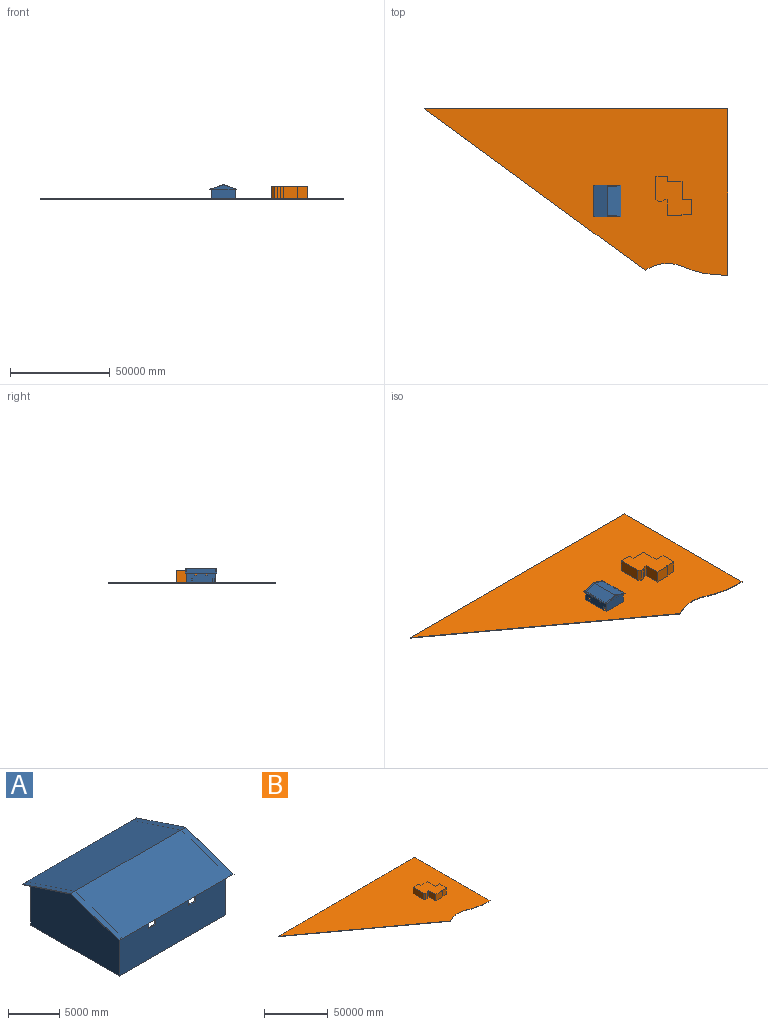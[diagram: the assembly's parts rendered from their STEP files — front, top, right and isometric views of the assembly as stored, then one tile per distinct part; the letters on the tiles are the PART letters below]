
ASSEMBLY  parts=2 mates=1
PART A: 51 faces, bbox 15849.6x13411.2x7112 mm
  f0: plane 13131.8x7065.43mm, normal (-1,0,0), area 73828293.2mm2, adj f2,f4,f8,f18,f19,f48,f49
  f1: plane 13131.8x7065.43mm, normal (1,0,0), area 51299306mm2, adj f2,f4,f5,f8,f10,f11,f12,f13
  f2: plane 14630.4x12192mm, normal (0,0,-1), area 4305959.1mm2, adj f0,f1,f3,f4,f6,f7,f8,f9
  f3: plane 14351x4876.8mm, normal (0,-1,0), area 65527610.9mm2, adj f2,f5,f6,f9,f17,f22,f23,f24
  f4: plane 14630.4x4876.8mm, normal (0,1,0), area 66890188.8mm2, adj f0,f1,f2,f5,f18,f22,f23,f24
  f5: plane 12954x2133.6mm, normal (0,0,-1), area 2088221.6mm2, adj f1,f3,f4,f6,f14,f36
  f6: plane 11912.6x4876.8mm, normal (-1,0,0), area 35566380.5mm2, adj f2,f3,f5,f7,f10,f11,f12,f13
  f7: plane 14351x4876.8mm, normal (0,1,0), area 68314702.1mm2, adj f2,f6,f9,f17,f37,f38,f39,f40
  f8: plane 14630.4x4876.8mm, normal (0,-1,0), area 69677280mm2, adj f0,f1,f2,f19,f37,f38,f39,f40
  f9: plane 11912.6x4876.8mm, normal (1,0,0), area 58095367.7mm2, adj f2,f3,f7,f17
  f10: plane 609.6x139.7mm, normal (0,0,-1), area 85161.1mm2, adj f1,f6,f12,f16
  f11: plane 4267.2x139.7mm, normal (0,1,0), area 596127.8mm2, adj f1,f2,f6,f13
  f12: plane 4267.2x139.7mm, normal (0,-1,0), area 596127.8mm2, adj f1,f6,f10,f13
  f13: plane 4876.8x139.7mm, normal (0,0,-1), area 681289mm2, adj f1,f6,f11,f12
  f14: plane 1879.6x139.7mm, normal (0,-1,0), area 262580.1mm2, adj f1,f5,f6,f15
  f15: plane 914.4x139.7mm, normal (0,0,-1), area 127741.7mm2, adj f1,f6,f14,f16
  f16: plane 1879.6x139.7mm, normal (0,1,0), area 262580.1mm2, adj f1,f6,f10,f15
  f17: plane 14351x11912.6mm, normal (0,0,-1), area 170957722.6mm2, adj f3,f6,f7,f9
  f18: plane 15849.6x609.6mm, normal (0,0,-1), area 9089014.1mm2, adj f0,f1,f4,f20,f45,f47,f48,f50
  f19: plane 15849.6x609.6mm, normal (0,0,-1), area 9089014.1mm2, adj f0,f1,f8,f21,f46,f47,f49,f50
  f20: plane 15849.6x6705.6mm, normal (0,0.32,0.95), area 112030092.6mm2, adj f18,f21,f47,f50
  f21: plane 15849.6x6705.6mm, normal (0,-0.32,0.95), area 112030092.6mm2, adj f19,f20,f47,f50
  f22: plane 914.4x139.7mm, normal (0,0,-1), area 127741.7mm2, adj f3,f4,f23,f25
  f23: plane 914.4x139.7mm, normal (-1,0,0), area 127741.7mm2, adj f3,f4,f22,f24
  f24: plane 914.4x139.7mm, normal (0,0,1), area 127741.7mm2, adj f3,f4,f23,f25
  f25: plane 914.4x139.7mm, normal (1,0,0), area 127741.7mm2, adj f3,f4,f22,f24
  f26: plane 914.4x139.7mm, normal (0,0,-1), area 127741.7mm2, adj f3,f4,f27,f29
  f27: plane 914.4x139.7mm, normal (-1,0,0), area 127741.7mm2, adj f3,f4,f26,f28
  f28: plane 914.4x139.7mm, normal (0,0,1), area 127741.7mm2, adj f3,f4,f27,f29
  f29: plane 914.4x139.7mm, normal (1,0,0), area 127741.7mm2, adj f3,f4,f26,f28
  f30: plane 914.4x139.7mm, normal (0,0,-1), area 127741.7mm2, adj f3,f4,f31,f33
  f31: plane 914.4x139.7mm, normal (-1,0,0), area 127741.7mm2, adj f3,f4,f30,f32
  f32: plane 914.4x139.7mm, normal (0,0,1), area 127741.7mm2, adj f3,f4,f31,f33
  f33: plane 914.4x139.7mm, normal (1,0,0), area 127741.7mm2, adj f3,f4,f30,f32
  f34: plane 2133.6x139.7mm, normal (1,0,0), area 298063.9mm2, adj f2,f3,f4,f35
  f35: plane 914.4x139.7mm, normal (0,0,-1), area 127741.7mm2, adj f3,f4,f34,f36
  f36: plane 2133.6x139.7mm, normal (-1,0,0), area 298063.9mm2, adj f3,f4,f5,f35
  f37: plane 914.4x139.7mm, normal (0,0,-1), area 127741.7mm2, adj f7,f8,f38,f39
  f38: plane 914.4x139.7mm, normal (-1,0,0), area 127741.7mm2, adj f7,f8,f37,f40
  f39: plane 914.4x139.7mm, normal (1,0,0), area 127741.7mm2, adj f7,f8,f37,f40
  f40: plane 914.4x139.7mm, normal (0,0,1), area 127741.7mm2, adj f7,f8,f38,f39
  f41: plane 914.4x139.7mm, normal (1,0,0), area 127741.7mm2, adj f7,f8,f42,f43
  f42: plane 914.4x139.7mm, normal (0,0,-1), area 127741.7mm2, adj f7,f8,f41,f44
  f43: plane 914.4x139.7mm, normal (0,0,1), area 127741.7mm2, adj f7,f8,f41,f44
  f44: plane 914.4x139.7mm, normal (-1,0,0), area 127741.7mm2, adj f7,f8,f42,f43
  f45: plane 6565.9x2188.63mm, normal (0,-0.32,-0.95), area 4219082mm2, adj f1,f18,f46,f47
  f46: plane 6565.9x2188.63mm, normal (0,0.32,-0.95), area 4219082mm2, adj f1,f19,f45,f47
  f47: plane 13411.2x2235.2mm, normal (1,0,0), area 618009.5mm2, adj f18,f19,f20,f21,f45,f46
  f48: plane 6565.9x2188.63mm, normal (0,-0.32,-0.95), area 4219082mm2, adj f0,f18,f49,f50
  f49: plane 6565.9x2188.63mm, normal (0,0.32,-0.95), area 4219082mm2, adj f0,f19,f48,f50
  f50: plane 13411.2x2235.2mm, normal (-1,0,0), area 618009.5mm2, adj f18,f19,f20,f21,f48,f49
PART B: 24 faces, bbox 152120x83370x6400.8 mm
  f0: plane 152120x83370mm, normal (0,0,1), area 7580944650.6mm2, adj f1,f2,f3,f4,f5,f6,f8,f9
  f1: plane 152120x304.8mm, normal (0,1,0), area 46366176mm2, adj f0,f2,f6,f7
  f2: plane 110759.25x81038.31mm, normal (-0.59,-0.81,0), area 41830752mm2, adj f0,f1,f3,f7
  f3: cylinder r=20000mm len=19224.83mm, axis (0,0,-1), area 6142188.7mm2, adj f0,f2,f4,f7
  f4: cylinder r=50000mm len=19925.93mm, axis (0,0,-1), area 6246891.5mm2, adj f0,f3,f5,f7
  f5: plane 2210x304.8mm, normal (0,-1,0), area 673608mm2, adj f0,f4,f6,f7
  f6: plane 83370x304.8mm, normal (1,0,0), area 25411176mm2, adj f0,f1,f5,f7
  f7: plane 152120x83370mm, normal (0,0,-1), area 7814443516.1mm2, adj f1,f2,f3,f4,f5,f6
  f8: plane 7380x6096mm, normal (0,1,0), area 44988480mm2, adj f0,f9,f22,f23
  f9: plane 6096x2608.06mm, normal (1,0,0), area 15898702.9mm2, adj f0,f8,f10,f23
  f10: plane 6096x5689.56mm, normal (0,1,0), area 34683564.6mm2, adj f0,f9,f11,f23
  f11: plane 11610x6096mm, normal (-1,0,0), area 70774560mm2, adj f0,f10,f12,f23
  f12: plane 6096x1209.33mm, normal (-0.72,-0.7,0), area 10302240mm2, adj f0,f11,f13,f23
  f13: plane 6096x1740mm, normal (0,-1,0), area 10607040mm2, adj f0,f12,f14,f23
  f14: plane 6096x1359.04mm, normal (0.6,-0.8,0), area 10363200mm2, adj f0,f13,f15,f23
  f15: plane 6096x1380mm, normal (0,-1,0), area 8412480mm2, adj f0,f14,f16,f23
  f16: plane 7930x6096mm, normal (-1,0,0), area 48341280mm2, adj f0,f15,f17,f23
  f17: plane 7390x6096mm, normal (0,-1,0), area 45049440mm2, adj f0,f16,f18,f23
  f18: plane 6096x600mm, normal (1,0,0), area 3657600mm2, adj f0,f17,f19,f23
  f19: plane 6096x4880mm, normal (0,-1,0), area 29748480mm2, adj f0,f18,f20,f23
  f20: plane 7580x6096mm, normal (1,0,0), area 46207680mm2, adj f0,f19,f21,f23
  f21: plane 6096x4860mm, normal (0,1,0), area 29626560mm2, adj f0,f20,f22,f23
  f22: plane 8940x6096mm, normal (1,0,0), area 54498240mm2, adj f0,f8,f21,f23
  f23: plane 19728.06x17929.56mm, normal (0,0,1), area 233498865.5mm2, adj f8,f9,f10,f11,f12,f13,f14,f15
PLACE A rot(axis=(0,0,1),90deg) t=(-24968.59,-4403,35428.44)mm
PLACE B t=(35374.97,41833.44,35123.64)mm fixed
MATE planar A.f0 <-> B.f17  axis (0,-1,0) through (-24968.59,-11718.2,38483.47)mm
